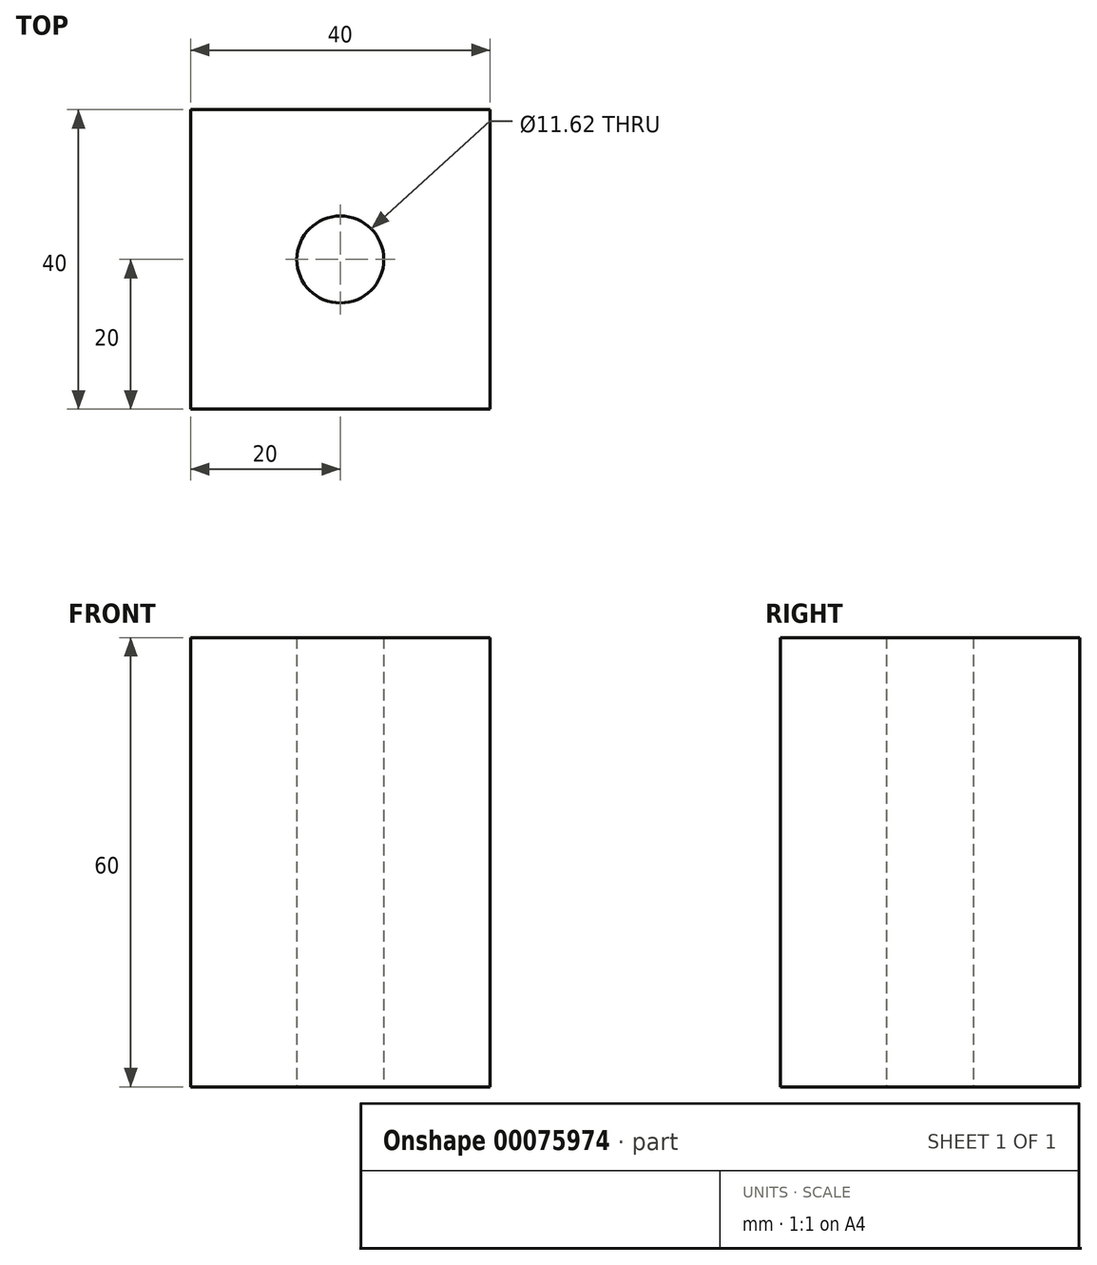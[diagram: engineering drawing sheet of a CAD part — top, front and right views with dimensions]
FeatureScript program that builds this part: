
annotation { "Feature Type Name" : "Feature", "Feature Type Description" : "" }
export const myFeature = defineFeature(function(context is Context, id is Id, definition is map)
    precondition{}
    {
        {
            var Q0;
            Q0=qCreatedBy(makeId("Top.planeOp"),FACE);
            var sketch = newSketch(context, id + "F0", { "sketchPlane" : qUnion([Q0])});
            skLineSegment(sketch, "E0.bottom", {"start": v(20, -20) * mm, "end": v(-20, -20) * mm});
            skLineSegment(sketch, "E0.top", {"start": v(20, 20) * mm, "end": v(-20, 20) * mm});
            skLineSegment(sketch, "E0.left", {"start": v(20, -20) * mm, "end": v(20, 20) * mm});
            skLineSegment(sketch, "E0.right", {"start": v(-20, -20) * mm, "end": v(-20, 20) * mm});
            skPoint(sketch, "E0.middle", {"position": v(0, 0) * mm});
            skCircle(sketch, "E1", {"center": v(0, 0) * mm, "radius": 5.81 * mm});
            skSolve(sketch);
        }
        {
            var Q0;
            Q0=makeQuery(id+"F0.imprint","IMPRINT",FACE,{"disambiguationData":[TD([[makeQuery(id+"F0.imprint","IMPRINT",EDGE,{"derivedFrom":sQuery(id+"F0.wireOp",EDGE,"E0.bottom")}),-1.0]])]});
            extrude(context, id + "F1", {"entities" : qUnion([Q0]), "depth" : 60 * mm});
        }
    });
